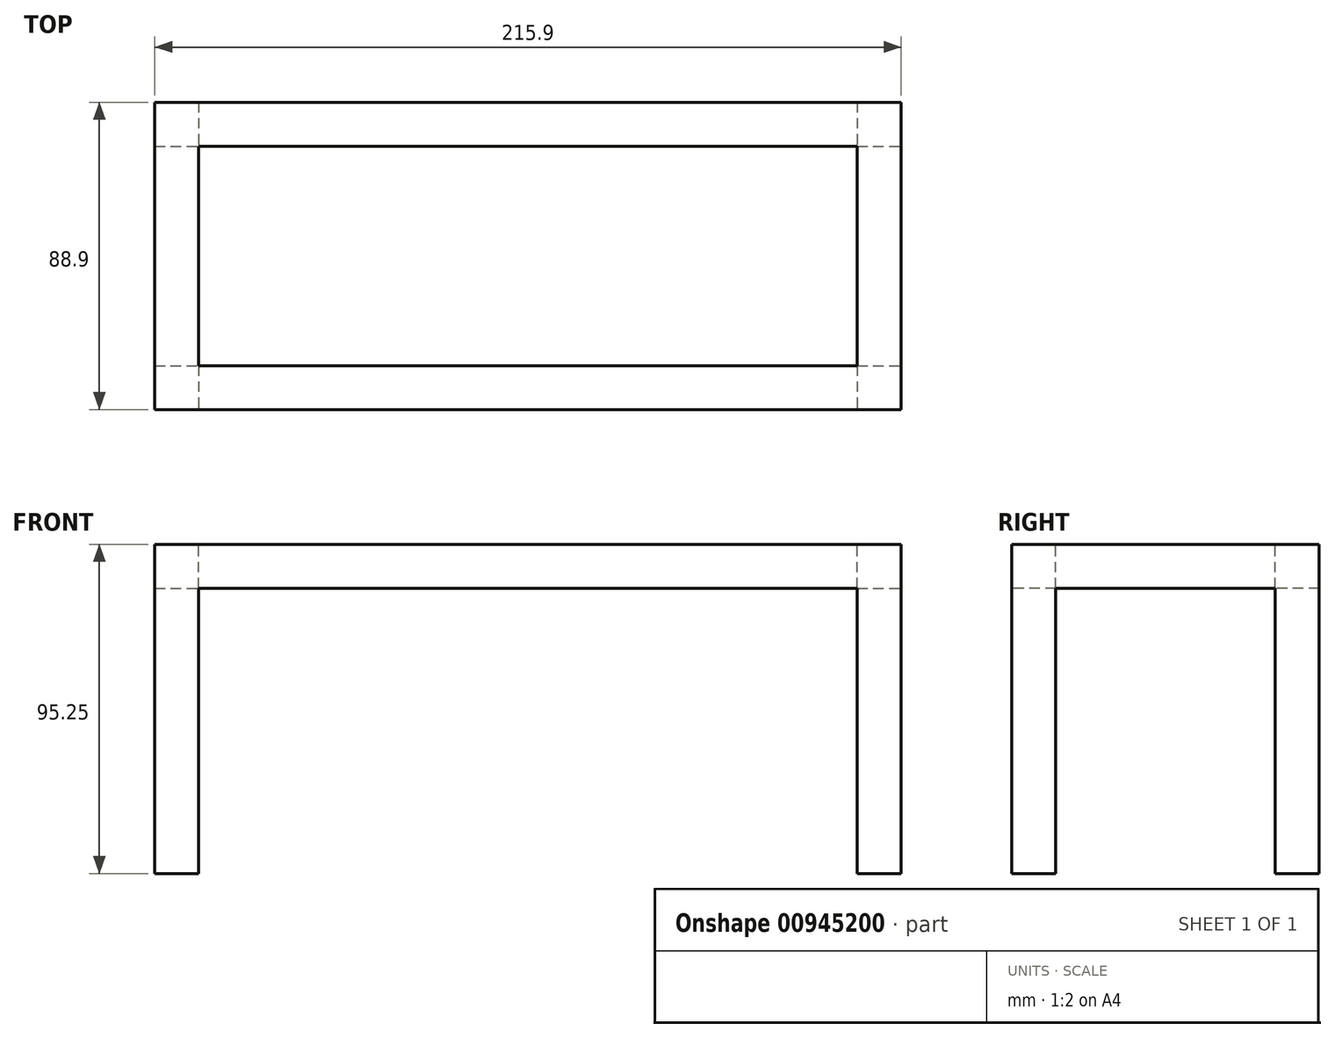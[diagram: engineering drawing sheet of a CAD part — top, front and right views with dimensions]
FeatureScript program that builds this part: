
annotation { "Feature Type Name" : "Feature", "Feature Type Description" : "" }
export const myFeature = defineFeature(function(context is Context, id is Id, definition is map)
    precondition{}
    {
        {
            var Q0;
            Q0=qCreatedBy(makeId("Top.planeOp"),FACE);
            var sketch = newSketch(context, id + "F0", { "sketchPlane" : qUnion([Q0])});
            skLineSegment(sketch, "E0.bottom", {"start": v(-224.84, 86.23) * mm, "end": v(-8.94, 86.23) * mm});
            skLineSegment(sketch, "E0.top", {"start": v(-224.84, -2.67) * mm, "end": v(-8.94, -2.67) * mm});
            skLineSegment(sketch, "E0.left", {"start": v(-224.84, 86.23) * mm, "end": v(-224.84, -2.67) * mm});
            skLineSegment(sketch, "E0.right", {"start": v(-8.94, 86.23) * mm, "end": v(-8.94, -2.67) * mm});
            skSolve(sketch);
        }
        {
            var Q0;
            Q0=makeQuery(id+"F0.imprint","IMPRINT",FACE,{"disambiguationData":[TD([[makeQuery(id+"F0.imprint","IMPRINT",EDGE,{"derivedFrom":sQuery(id+"F0.wireOp",EDGE,"E0.bottom")}),-1.0]])]});
            extrude(context, id + "F1", {"entities" : qUnion([Q0]), "depth" : 95.25 * mm, "offsetDistance" : 25.4 * mm});
        }
        {
            var Q0;
            Q0=makeQuery(id+"F1.opExtrude","CAP_FACE",FACE,{"disambiguationData":[OSD([sQuery(id+"F0.wireOp",EDGE,"E0.bottom"),sQuery(id+"F0.wireOp",EDGE,"E0.top"),sQuery(id+"F0.wireOp",EDGE,"E0.left"),sQuery(id+"F0.wireOp",EDGE,"E0.right")])],"isStart":false});
            var sketch = newSketch(context, id + "F2", { "sketchPlane" : qUnion([Q0])});
            skLineSegment(sketch, "E1.bottom", {"start": v(-224.84, 86.23) * mm, "end": v(-212.14, 86.23) * mm});
            skLineSegment(sketch, "E1.top", {"start": v(-224.84, -2.67) * mm, "end": v(-212.14, -2.67) * mm});
            skLineSegment(sketch, "E1.left", {"start": v(-224.84, 86.23) * mm, "end": v(-224.84, -2.67) * mm});
            skLineSegment(sketch, "E1.right", {"start": v(-212.14, 86.23) * mm, "end": v(-212.14, -2.67) * mm});
            skLineSegment(sketch, "E2.bottom", {"start": v(-8.94, 86.23) * mm, "end": v(-21.64, 86.23) * mm});
            skLineSegment(sketch, "E2.top", {"start": v(-8.94, -2.67) * mm, "end": v(-21.64, -2.67) * mm});
            skLineSegment(sketch, "E2.left", {"start": v(-8.94, 86.23) * mm, "end": v(-8.94, -2.67) * mm});
            skLineSegment(sketch, "E2.right", {"start": v(-21.64, 86.23) * mm, "end": v(-21.64, -2.67) * mm});
            skLineSegment(sketch, "E3.bottom", {"start": v(-224.84, 86.23) * mm, "end": v(-8.94, 86.23) * mm});
            skLineSegment(sketch, "E3.top", {"start": v(-224.84, 73.53) * mm, "end": v(-8.94, 73.53) * mm});
            skLineSegment(sketch, "E3.left", {"start": v(-224.84, 86.23) * mm, "end": v(-224.84, 73.53) * mm});
            skLineSegment(sketch, "E3.right", {"start": v(-8.94, 86.23) * mm, "end": v(-8.94, 73.53) * mm});
            skLineSegment(sketch, "E4.bottom", {"start": v(-224.84, -2.67) * mm, "end": v(-8.94, -2.67) * mm});
            skLineSegment(sketch, "E4.top", {"start": v(-224.84, 10.03) * mm, "end": v(-8.94, 10.03) * mm});
            skLineSegment(sketch, "E4.left", {"start": v(-224.84, -2.67) * mm, "end": v(-224.84, 10.03) * mm});
            skLineSegment(sketch, "E4.right", {"start": v(-8.94, -2.67) * mm, "end": v(-8.94, 10.03) * mm});
            skSolve(sketch);
        }
        {
            var Q0;
            {var subQ0=sQuery(id+"F2.wireOp",EDGE,"E3.top");var subQ1=sQuery(id+"F2.wireOp",EDGE,"E1.right");var subQ2=makeQuery(id+"F2.imprint","INTERSECT",VERTEX,{"derivedFrom":[subQ1,subQ0]});Q0=makeQuery(id+"F2.imprint","IMPRINT",FACE,{"disambiguationData":[TD([[makeQuery(id+"F2.imprint","IMPRINT",EDGE,{"disambiguationData":[TD([[subQ2,-1.0]])],"derivedFrom":subQ1}),1.0]])]});}
            extrude(context, id + "F3", {"entities" : qUnion([Q0]), "operationType" : NewBodyOperationType.REMOVE, "endBound" : BoundingType.THROUGH_ALL, "oppositeDirection" : true, "depth" : 25.4 * mm, "offsetDistance" : 25.4 * mm});
        }
        {
            var Q0;
            Q0=makeQuery(id+"F1.opExtrude","SWEPT_FACE",FACE,{"disambiguationData":[OSD([sQuery(id+"F0.wireOp",EDGE,"E0.top")])]});
            var sketch = newSketch(context, id + "F4", { "sketchPlane" : qUnion([Q0])});
            skLineSegment(sketch, "E5.bottom", {"start": v(-224.84, 0) * mm, "end": v(-212.14, 0) * mm});
            skLineSegment(sketch, "E5.top", {"start": v(-224.84, 95.25) * mm, "end": v(-212.14, 95.25) * mm});
            skLineSegment(sketch, "E5.left", {"start": v(-224.84, 0) * mm, "end": v(-224.84, 95.25) * mm});
            skLineSegment(sketch, "E5.right", {"start": v(-212.14, 0) * mm, "end": v(-212.14, 95.25) * mm});
            skLineSegment(sketch, "E6.bottom", {"start": v(-8.94, 0) * mm, "end": v(-21.64, 0) * mm});
            skLineSegment(sketch, "E6.top", {"start": v(-8.94, 95.25) * mm, "end": v(-21.64, 95.25) * mm});
            skLineSegment(sketch, "E6.left", {"start": v(-8.94, 0) * mm, "end": v(-8.94, 95.25) * mm});
            skLineSegment(sketch, "E6.right", {"start": v(-21.64, 0) * mm, "end": v(-21.64, 95.25) * mm});
            skLineSegment(sketch, "E7.bottom", {"start": v(-224.84, 95.25) * mm, "end": v(-8.94, 95.25) * mm});
            skLineSegment(sketch, "E7.top", {"start": v(-224.84, 82.55) * mm, "end": v(-8.94, 82.55) * mm});
            skLineSegment(sketch, "E7.left", {"start": v(-224.84, 95.25) * mm, "end": v(-224.84, 82.55) * mm});
            skLineSegment(sketch, "E7.right", {"start": v(-8.94, 95.25) * mm, "end": v(-8.94, 82.55) * mm});
            skLineSegment(sketch, "E8.bottom", {"start": v(-212.14, 0) * mm, "end": v(-21.64, 0) * mm});
            skLineSegment(sketch, "E8.top", {"start": v(-212.14, 82.55) * mm, "end": v(-21.64, 82.55) * mm});
            skLineSegment(sketch, "E8.left", {"start": v(-212.14, 0) * mm, "end": v(-212.14, 82.55) * mm});
            skLineSegment(sketch, "E8.right", {"start": v(-21.64, 0) * mm, "end": v(-21.64, 82.55) * mm});
            skSolve(sketch);
        }
        {
            var Q0;
            {var subQ0=sQuery(id+"F4.wireOp",EDGE,"E8.bottom");Q0=makeQuery(id+"F4.imprint","IMPRINT",FACE,{"disambiguationData":[TD([[makeQuery(id+"F4.imprint","IMPRINT",EDGE,{"derivedFrom":subQ0}),1.0]])]});}
            extrude(context, id + "F5", {"entities" : qUnion([Q0]), "operationType" : NewBodyOperationType.REMOVE, "endBound" : BoundingType.THROUGH_ALL, "oppositeDirection" : true, "depth" : 25.4 * mm, "offsetDistance" : 25.4 * mm});
        }
        {
            var Q0;
            Q0=makeQuery(id+"F1.opExtrude","SWEPT_FACE",FACE,{"disambiguationData":[OSD([sQuery(id+"F0.wireOp",EDGE,"E0.right")])]});
            var sketch = newSketch(context, id + "F6", { "sketchPlane" : qUnion([Q0])});
            skLineSegment(sketch, "E9.bottom", {"start": v(-2.67, 0) * mm, "end": v(10.03, 0) * mm});
            skLineSegment(sketch, "E9.top", {"start": v(-2.67, 95.25) * mm, "end": v(10.03, 95.25) * mm});
            skLineSegment(sketch, "E9.left", {"start": v(-2.67, 0) * mm, "end": v(-2.67, 95.25) * mm});
            skLineSegment(sketch, "E9.right", {"start": v(10.03, 0) * mm, "end": v(10.03, 95.25) * mm});
            skLineSegment(sketch, "E10.bottom", {"start": v(86.23, 0) * mm, "end": v(73.53, 0) * mm});
            skLineSegment(sketch, "E10.top", {"start": v(86.23, 95.25) * mm, "end": v(73.53, 95.25) * mm});
            skLineSegment(sketch, "E10.left", {"start": v(86.23, 0) * mm, "end": v(86.23, 95.25) * mm});
            skLineSegment(sketch, "E10.right", {"start": v(73.53, 0) * mm, "end": v(73.53, 95.25) * mm});
            skLineSegment(sketch, "E11.bottom", {"start": v(-2.67, 95.25) * mm, "end": v(86.23, 95.25) * mm});
            skLineSegment(sketch, "E11.top", {"start": v(-2.67, 82.55) * mm, "end": v(86.23, 82.55) * mm});
            skLineSegment(sketch, "E11.left", {"start": v(-2.67, 95.25) * mm, "end": v(-2.67, 82.55) * mm});
            skLineSegment(sketch, "E11.right", {"start": v(86.23, 95.25) * mm, "end": v(86.23, 82.55) * mm});
            skLineSegment(sketch, "E12.bottom", {"start": v(10.03, 82.55) * mm, "end": v(73.53, 82.55) * mm});
            skLineSegment(sketch, "E12.top", {"start": v(10.03, 0) * mm, "end": v(73.53, 0) * mm});
            skLineSegment(sketch, "E12.left", {"start": v(10.03, 82.55) * mm, "end": v(10.03, 0) * mm});
            skLineSegment(sketch, "E12.right", {"start": v(73.53, 82.55) * mm, "end": v(73.53, 0) * mm});
            skSolve(sketch);
        }
        {
            var Q0;
            {var subQ0=sQuery(id+"F6.wireOp",EDGE,"E12.top");Q0=makeQuery(id+"F6.imprint","IMPRINT",FACE,{"disambiguationData":[TD([[makeQuery(id+"F6.imprint","IMPRINT",EDGE,{"derivedFrom":subQ0}),-1.0]])]});}
            extrude(context, id + "F7", {"entities" : qUnion([Q0]), "operationType" : NewBodyOperationType.REMOVE, "endBound" : BoundingType.THROUGH_ALL, "oppositeDirection" : true, "depth" : 25.4 * mm, "offsetDistance" : 25.4 * mm});
        }
    });
